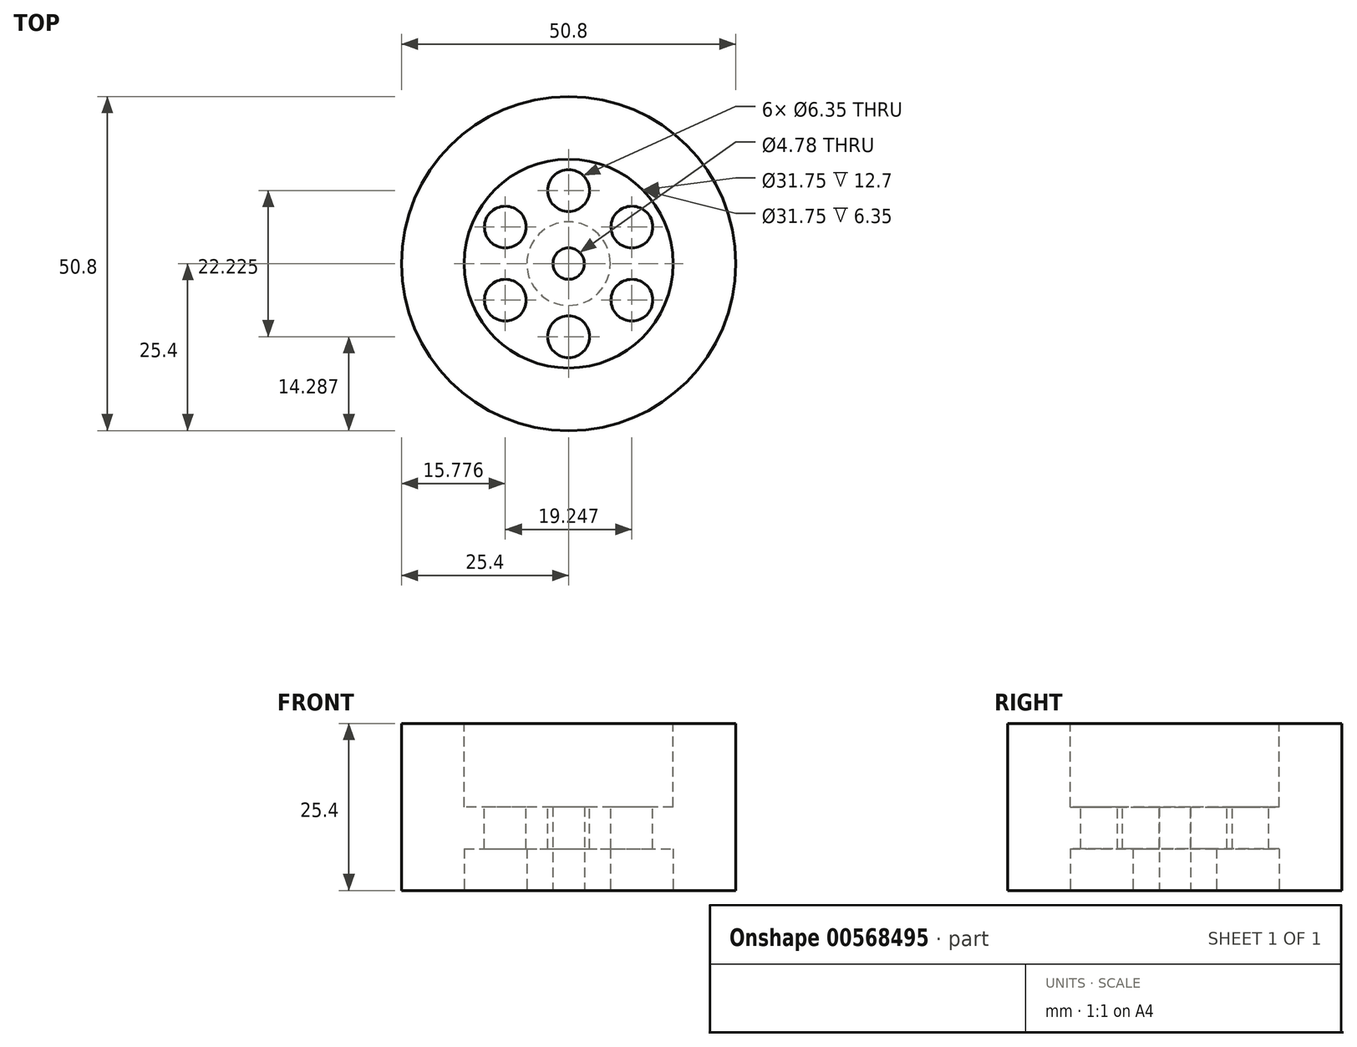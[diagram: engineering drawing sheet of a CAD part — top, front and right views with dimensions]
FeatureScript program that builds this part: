
annotation { "Feature Type Name" : "Feature", "Feature Type Description" : "" }
export const myFeature = defineFeature(function(context is Context, id is Id, definition is map)
    precondition{}
    {
        {
            var Q0;
            Q0=qCreatedBy(makeId("Top.planeOp"),FACE);
            var sketch = newSketch(context, id + "F0", { "sketchPlane" : qUnion([Q0])});
            skCircle(sketch, "E0", {"center": v(0, 0) * mm, "radius": 25.4 * mm});
            skCircle(sketch, "E1", {"center": v(0, 0) * mm, "radius": 2.39 * mm});
            skSolve(sketch);
        }
        {
            var Q0;
            Q0 = qSketchRegion(id + "F0", true);
            extrude(context, id + "F1", {"entities" : qUnion([Q0]), "depth" : 25.4 * mm, "offsetDistance" : 25.4 * mm});
        }
        {
            var Q0;
            Q0=makeQuery(id+"F1.opExtrude","CAP_FACE",FACE,{"disambiguationData":[OSD([sQuery(id+"F0.wireOp",EDGE,"E0"),sQuery(id+"F0.wireOp",EDGE,"E1")])],"isStart":false});
            var sketch = newSketch(context, id + "F2", { "sketchPlane" : qUnion([Q0])});
            skCircle(sketch, "E2", {"center": v(0, 0) * mm, "radius": 15.88 * mm});
            skSolve(sketch);
        }
        {
            var Q0;
            Q0 = qSketchRegion(id + "F2", true);
            extrude(context, id + "F3", {"entities" : qUnion([Q0]), "operationType" : NewBodyOperationType.REMOVE, "oppositeDirection" : true, "depth" : 12.7 * mm, "offsetDistance" : 25.4 * mm});
        }
        {
            var Q0;
            Q0=makeQuery(id+"F1.opExtrude","CAP_FACE",FACE,{"disambiguationData":[OSD([sQuery(id+"F0.wireOp",EDGE,"E0"),sQuery(id+"F0.wireOp",EDGE,"E1")])],"isStart":true});
            var sketch = newSketch(context, id + "F4", { "sketchPlane" : qUnion([Q0])});
            skCircle(sketch, "E3", {"center": v(0, 0) * mm, "radius": 15.88 * mm});
            skCircle(sketch, "E4", {"center": v(0, 0) * mm, "radius": 6.35 * mm});
            skSolve(sketch);
        }
        {
            var Q0;
            Q0 = qSketchRegion(id + "F4", true);
            extrude(context, id + "F5", {"entities" : qUnion([Q0]), "operationType" : NewBodyOperationType.REMOVE, "oppositeDirection" : true, "depth" : 6.35 * mm, "offsetDistance" : 25.4 * mm});
        }
        {
            var Q0;
            Q0=makeQuery(id+"F3.boolean.opBoolean","COPY",FACE,{"derivedFrom":makeQuery(id+"F3.opExtrude","CAP_FACE",FACE,{"disambiguationData":[OSD([sQuery(id+"F2.wireOp",EDGE,"E2")])],"isStart":false})});
            var sketch = newSketch(context, id + "F6", { "sketchPlane" : qUnion([Q0])});
            skCircle(sketch, "E5", {"center": v(0, 0) * mm, "radius": 11.11 * mm});
            skCircle(sketch, "E6", {"center": v(0, 11.11) * mm, "radius": 3.18 * mm});
            skCircle(sketch, "E7.1.0", {"center": v(-9.62, 5.56) * mm, "radius": 3.18 * mm});
            skCircle(sketch, "E7.2.0", {"center": v(-9.62, -5.56) * mm, "radius": 3.18 * mm});
            skCircle(sketch, "E7.3.0", {"center": v(0, -11.11) * mm, "radius": 3.18 * mm});
            skCircle(sketch, "E7.4.0", {"center": v(9.62, -5.56) * mm, "radius": 3.18 * mm});
            skCircle(sketch, "E7.5.0", {"center": v(9.62, 5.56) * mm, "radius": 3.18 * mm});
            skSolve(sketch);
        }
        {
            var Q0;
            Q0=makeQuery(id+"F6.imprint","IMPRINT",FACE,{"disambiguationData":[TD([[makeQuery(id+"F6.imprint","IMPRINT",EDGE,{"derivedFrom":makeQuery(id+"F3.boolean.opBoolean","INTERSECT",EDGE,{"derivedFrom":[makeQuery(id+"F1.opExtrude","SWEPT_FACE",FACE,{"disambiguationData":[OSD([sQuery(id+"F0.wireOp",EDGE,"E1")])]}),makeQuery(id+"F3.opExtrude","CAP_FACE",FACE,{"disambiguationData":[OSD([sQuery(id+"F2.wireOp",EDGE,"E2")])],"isStart":false})]})}),1.0]])]});
            var Q1;
            {var subQ0=sQuery(id+"F6.wireOp",EDGE,"E7.5.0");var subQ1=sQuery(id+"F6.wireOp",EDGE,"E5");var subQ2=makeQuery(id+"F6.imprint","INTERSECT",VERTEX,{"disambiguationData":[OD(0.0)],"derivedFrom":[subQ1,subQ0]});Q1=makeQuery(id+"F6.imprint","IMPRINT",FACE,{"disambiguationData":[TD([[makeQuery(id+"F6.imprint","IMPRINT",EDGE,{"disambiguationData":[TD([[subQ2,1.0]])],"derivedFrom":subQ1}),1.0]])]});}
            var Q2;
            {var subQ0=sQuery(id+"F6.wireOp",EDGE,"E7.5.0");var subQ1=sQuery(id+"F6.wireOp",EDGE,"E5");var subQ2=makeQuery(id+"F6.imprint","INTERSECT",VERTEX,{"disambiguationData":[OD(0.0)],"derivedFrom":[subQ1,subQ0]});Q2=makeQuery(id+"F6.imprint","IMPRINT",FACE,{"disambiguationData":[TD([[makeQuery(id+"F6.imprint","IMPRINT",EDGE,{"disambiguationData":[TD([[subQ2,1.0]])],"derivedFrom":subQ1}),-1.0]])]});}
            var Q3;
            {var subQ0=sQuery(id+"F6.wireOp",EDGE,"E6");var subQ1=sQuery(id+"F6.wireOp",EDGE,"E5");var subQ2=makeQuery(id+"F6.imprint","INTERSECT",VERTEX,{"disambiguationData":[OD(0.0)],"derivedFrom":[subQ1,subQ0]});Q3=makeQuery(id+"F6.imprint","IMPRINT",FACE,{"disambiguationData":[TD([[makeQuery(id+"F6.imprint","IMPRINT",EDGE,{"disambiguationData":[TD([[subQ2,-1.0]])],"derivedFrom":subQ1}),1.0]])]});}
            var Q4;
            {var subQ0=sQuery(id+"F6.wireOp",EDGE,"E6");var subQ1=sQuery(id+"F6.wireOp",EDGE,"E5");var subQ2=makeQuery(id+"F6.imprint","INTERSECT",VERTEX,{"disambiguationData":[OD(0.0)],"derivedFrom":[subQ1,subQ0]});Q4=makeQuery(id+"F6.imprint","IMPRINT",FACE,{"disambiguationData":[TD([[makeQuery(id+"F6.imprint","IMPRINT",EDGE,{"disambiguationData":[TD([[subQ2,-1.0]])],"derivedFrom":subQ1}),-1.0]])]});}
            var Q5;
            {var subQ0=sQuery(id+"F6.wireOp",EDGE,"E7.1.0");var subQ1=sQuery(id+"F6.wireOp",EDGE,"E5");var subQ2=makeQuery(id+"F6.imprint","INTERSECT",VERTEX,{"disambiguationData":[OD(0.0)],"derivedFrom":[subQ1,subQ0]});Q5=makeQuery(id+"F6.imprint","IMPRINT",FACE,{"disambiguationData":[TD([[makeQuery(id+"F6.imprint","IMPRINT",EDGE,{"disambiguationData":[TD([[subQ2,-1.0]])],"derivedFrom":subQ1}),1.0]])]});}
            var Q6;
            {var subQ0=sQuery(id+"F6.wireOp",EDGE,"E7.1.0");var subQ1=sQuery(id+"F6.wireOp",EDGE,"E5");var subQ2=makeQuery(id+"F6.imprint","INTERSECT",VERTEX,{"disambiguationData":[OD(0.0)],"derivedFrom":[subQ1,subQ0]});Q6=makeQuery(id+"F6.imprint","IMPRINT",FACE,{"disambiguationData":[TD([[makeQuery(id+"F6.imprint","IMPRINT",EDGE,{"disambiguationData":[TD([[subQ2,-1.0]])],"derivedFrom":subQ1}),-1.0]])]});}
            var Q7;
            {var subQ0=sQuery(id+"F6.wireOp",EDGE,"E7.2.0");var subQ1=sQuery(id+"F6.wireOp",EDGE,"E5");var subQ2=makeQuery(id+"F6.imprint","INTERSECT",VERTEX,{"disambiguationData":[OD(0.0)],"derivedFrom":[subQ1,subQ0]});Q7=makeQuery(id+"F6.imprint","IMPRINT",FACE,{"disambiguationData":[TD([[makeQuery(id+"F6.imprint","IMPRINT",EDGE,{"disambiguationData":[TD([[subQ2,-1.0]])],"derivedFrom":subQ1}),1.0]])]});}
            var Q8;
            {var subQ0=sQuery(id+"F6.wireOp",EDGE,"E7.2.0");var subQ1=sQuery(id+"F6.wireOp",EDGE,"E5");var subQ2=makeQuery(id+"F6.imprint","INTERSECT",VERTEX,{"disambiguationData":[OD(0.0)],"derivedFrom":[subQ1,subQ0]});Q8=makeQuery(id+"F6.imprint","IMPRINT",FACE,{"disambiguationData":[TD([[makeQuery(id+"F6.imprint","IMPRINT",EDGE,{"disambiguationData":[TD([[subQ2,-1.0]])],"derivedFrom":subQ1}),-1.0]])]});}
            var Q9;
            {var subQ0=sQuery(id+"F6.wireOp",EDGE,"E7.3.0");var subQ1=sQuery(id+"F6.wireOp",EDGE,"E5");var subQ2=makeQuery(id+"F6.imprint","INTERSECT",VERTEX,{"disambiguationData":[OD(0.0)],"derivedFrom":[subQ1,subQ0]});Q9=makeQuery(id+"F6.imprint","IMPRINT",FACE,{"disambiguationData":[TD([[makeQuery(id+"F6.imprint","IMPRINT",EDGE,{"disambiguationData":[TD([[subQ2,-1.0]])],"derivedFrom":subQ1}),1.0]])]});}
            var Q10;
            {var subQ0=sQuery(id+"F6.wireOp",EDGE,"E7.3.0");var subQ1=sQuery(id+"F6.wireOp",EDGE,"E5");var subQ2=makeQuery(id+"F6.imprint","INTERSECT",VERTEX,{"disambiguationData":[OD(0.0)],"derivedFrom":[subQ1,subQ0]});Q10=makeQuery(id+"F6.imprint","IMPRINT",FACE,{"disambiguationData":[TD([[makeQuery(id+"F6.imprint","IMPRINT",EDGE,{"disambiguationData":[TD([[subQ2,-1.0]])],"derivedFrom":subQ1}),-1.0]])]});}
            var Q11;
            {var subQ0=sQuery(id+"F6.wireOp",EDGE,"E7.4.0");var subQ1=sQuery(id+"F6.wireOp",EDGE,"E5");var subQ2=makeQuery(id+"F6.imprint","INTERSECT",VERTEX,{"disambiguationData":[OD(0.0)],"derivedFrom":[subQ1,subQ0]});Q11=makeQuery(id+"F6.imprint","IMPRINT",FACE,{"disambiguationData":[TD([[makeQuery(id+"F6.imprint","IMPRINT",EDGE,{"disambiguationData":[TD([[subQ2,-1.0]])],"derivedFrom":subQ1}),1.0]])]});}
            var Q12;
            {var subQ0=sQuery(id+"F6.wireOp",EDGE,"E7.4.0");var subQ1=sQuery(id+"F6.wireOp",EDGE,"E5");var subQ2=makeQuery(id+"F6.imprint","INTERSECT",VERTEX,{"disambiguationData":[OD(0.0)],"derivedFrom":[subQ1,subQ0]});Q12=makeQuery(id+"F6.imprint","IMPRINT",FACE,{"disambiguationData":[TD([[makeQuery(id+"F6.imprint","IMPRINT",EDGE,{"disambiguationData":[TD([[subQ2,-1.0]])],"derivedFrom":subQ1}),-1.0]])]});}
            extrude(context, id + "F7", {"entities" : qUnion([Q0, Q1, Q2, Q3, Q4, Q5, Q6, Q7, Q8, Q9, Q10, Q11, Q12]), "operationType" : NewBodyOperationType.REMOVE, "endBound" : BoundingType.THROUGH_ALL, "oppositeDirection" : true, "depth" : 25.4 * mm, "offsetDistance" : 25.4 * mm});
        }
    });
